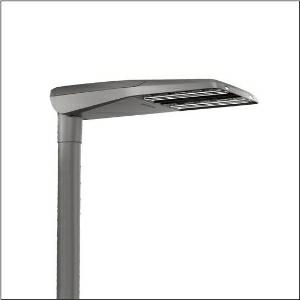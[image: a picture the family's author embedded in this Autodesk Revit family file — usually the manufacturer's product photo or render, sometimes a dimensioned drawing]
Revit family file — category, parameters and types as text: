
# Revit family: streetlight_sl_11_iq_midi___st1_0ab_5xc3n41f08le_a448
name_source: partatom
category: Lighting Fixtures
units: mm (PartAtom-declared; Revit-internal decimal feet)

## family parameters
Cut with Voids When Loaded = No
Host = Face
Light Source = No
Part Type = Normal
Room Calculation Point = No
Round Connector Dimension = Use Diameter
Shared = No

## types (1)
- --- (1 x LED, 8080 lm, 60.4 W, 4000K)
    Apparent Load = 60 VA
    CIE Flux Codes = 29 63 95 100 100
    Color Rendering = 70
    Color Temperature = 4000K
    Default Elevation = 1800 mm
    Description = Streetlight SL 11 iQ midi, mast luminaire, primary light control with 3 zone facetted reflector, of plastic, silver coated, highly specular, primary optical cover: cover, of PMMA, transparent, light distribution: ST1.0aB, light emission: direct distribution, primary light characteristic: asymmetric, installation type: post-top, side-entry, lamps: LED, High Power LED, rated values: 8.080lm | 60,4W | 133,8lm/W (begin service life); end service life: 8.080lm | 62,5W; at 50% lumin. flux: 4.040lm | 29,7W | 136lm/W, colour temperature: 4000K, colour rendering: CRI > 70, light colour: 740, light setting 1 begin service life: 100% | 8.080lm | 60,4W | 133,8lm/W | 4.000K, light setting 1 end service life: 62,5W, further light settings possible, control: optimised constant luminous flux control (CLO 2.0), Street-Remote, Desk-Remote (wireless, voltage-free reading and setting of iQ features in the workshop via application-optimized NFC function/RFID function), Light-Fading, Smart-Wire, Night-Set, Lumen-Switch, Temp-Guard, Auto-Match, with cable H07RN-F 5x 1.5mm², mains connection: 230..240V, AC, 50/60Hz, connection cable pre-assembled, cable length: 8,5m, luminaire housing, of diecast aluminium, powder-coated, Siteco® metallic grey (DB 702S), please order mast flange separately, inclination adjustable without tools: 0°, 5°, 10°, 15° (post-top) | 0°, -5°, -10°, -15° (side-entry), sealing non-destructively replaceable, multi-level sealing system, length: 780mm, width: 376mm, height: 118mm, mast flange for spigot size: 42mm (side-entry): 5XC10008XM4, 60/48mm (side-entry/post-top): 5XC10108XM2, 76/60mm (side-entry/post-top): 5XC10108XM1, equipment: standard, protection rating (complete): IP66, insulation class (complete): insulation class II (safety insulation), certification: CE, ENEC, ENEC+, VDE, impact resistance: IK10, permissible operating ambient temperature for outdoor applications: -25..+50°C, standard-compliant lighting for roads and squares, Environmental Product Declaration (EPD) tested and certified by an independent institute, packaging unit: 1 piece

Light Distribution: ST1.0aB
    Height = 118 mm
    Lamp = 1 x LED
    Lamp Light Flux = 8080 lm
    Lamp Power = 60.4 W
    Lamp count = 1
    Length = 780 mm
    Luminous efficacy = 134 lm/W
    Manufacturer = Siteco
    ModVariant = No
    Model = 5XC3N41F08LE
    Number of Poles = 1
    OnlyDefault = Yes
    Power Factor = 1
    Product Name = Streetlight SL 11 iQ midi | ST1.0aB
    Product group = mast luminaire | pylon top
    ProductGroupID = 6100
    Protection Class = Protection class II
    Protection Degree = IP 66
    RLX_Detail_Level = 1
    RLX_Emergency_Light_Flux = 0 lm
    RLX_Emergency_Type = 0
    RLX_Emergency_Type_DB = No
    RlxData = <blob elided: 70381 chars, md5=468bdc37>
    Socket = socket
    Standby Power = 0 W
    System Light Flux = 8080 lm
    System Power = 60 W
    Type Comments = factory setting: luminous flux: 100 % | dim-lin: 254 | 520 mA
    Type Image = l_1005960.jpg
    URL = http://relux.com
    VarID = @adj_109561
    Voltage = 0 V
    Weight = 0.00 kg
    Width = 376 mm

## geometry (parser evidence)
native form markers: Blend x4, Sweep x10
no freeform markers — native parametric forms only
